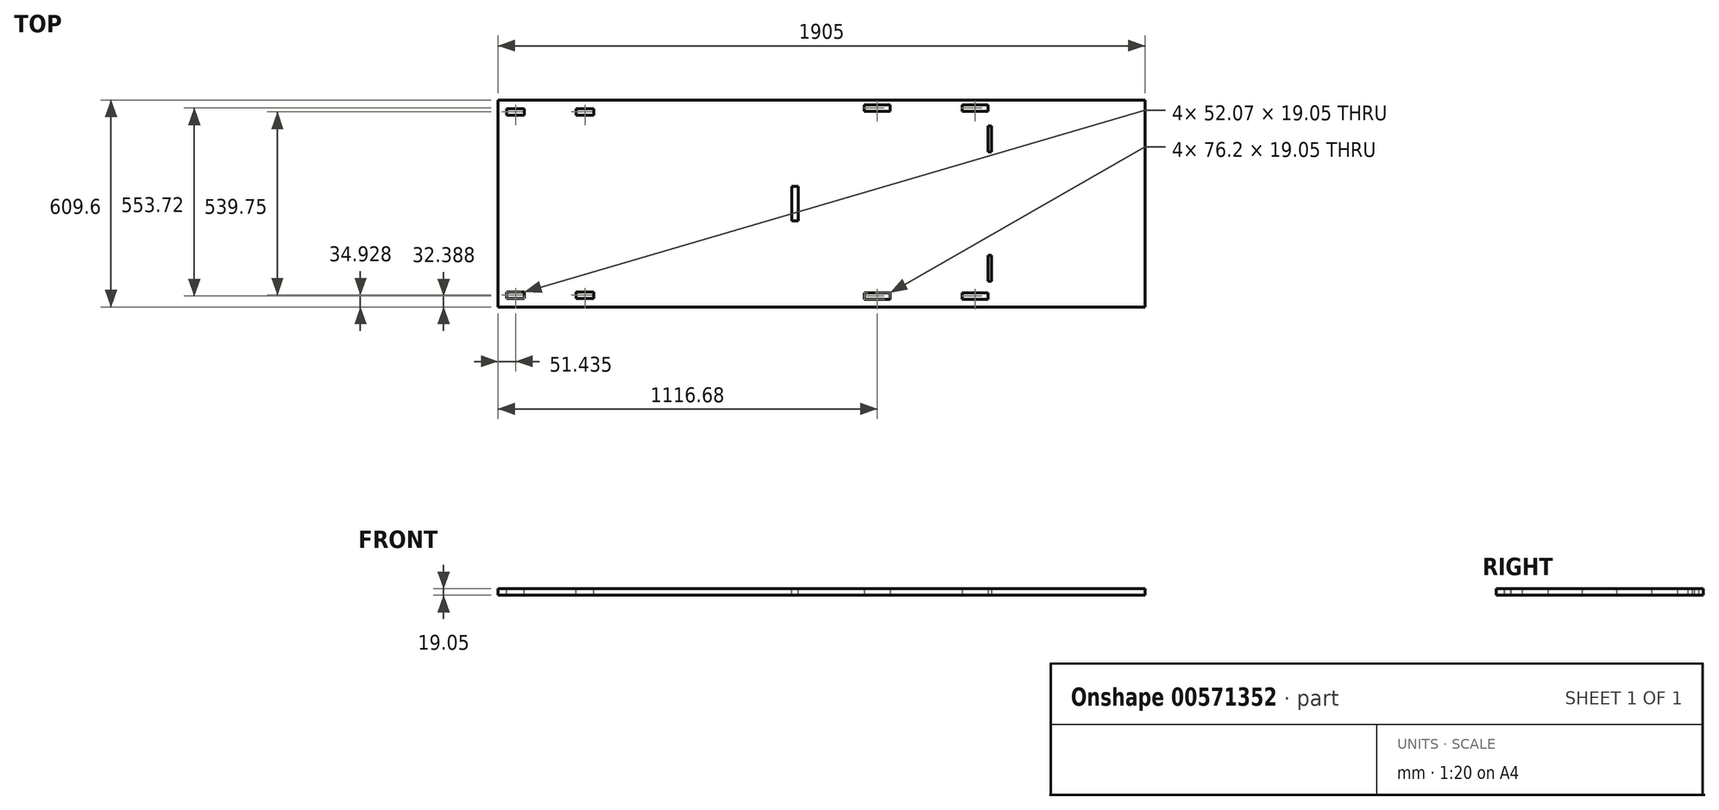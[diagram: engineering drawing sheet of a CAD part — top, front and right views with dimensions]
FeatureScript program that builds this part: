
annotation { "Feature Type Name" : "Feature", "Feature Type Description" : "" }
export const myFeature = defineFeature(function(context is Context, id is Id, definition is map)
    precondition{}
    {
        {
            var Q0;
            Q0=qCreatedBy(makeId("Top.planeOp"),FACE);
            var sketch = newSketch(context, id + "F0", { "sketchPlane" : qUnion([Q0])});
            skLineSegment(sketch, "E0.bottom", {"start": v(-750.92, 356.97) * mm, "end": v(1154.08, 356.97) * mm});
            skLineSegment(sketch, "E0.top", {"start": v(-750.92, -252.63) * mm, "end": v(1154.08, -252.63) * mm});
            skLineSegment(sketch, "E0.left", {"start": v(-750.92, 356.97) * mm, "end": v(-750.92, -252.63) * mm});
            skLineSegment(sketch, "E0.right", {"start": v(1154.08, 356.97) * mm, "end": v(1154.08, -252.63) * mm});
            skLineSegment(sketch, "E1", {"start": v(1154.08, 356.97) * mm, "end": v(696.88, 356.97) * mm});
            skLineSegment(sketch, "E2", {"start": v(691.34, 280.77) * mm, "end": v(691.34, 204.57) * mm});
            skLineSegment(sketch, "E3", {"start": v(701.5, 280.77) * mm, "end": v(701.5, 204.57) * mm});
            skLineSegment(sketch, "E4", {"start": v(691.34, 280.77) * mm, "end": v(701.5, 280.77) * mm});
            skLineSegment(sketch, "E5", {"start": v(691.34, 204.57) * mm, "end": v(701.5, 204.57) * mm});
            skLineSegment(sketch, "E6", {"start": v(701.5, -100.23) * mm, "end": v(701.5, -176.43) * mm});
            skLineSegment(sketch, "E7", {"start": v(691.34, -100.23) * mm, "end": v(691.34, -176.43) * mm});
            skLineSegment(sketch, "E8", {"start": v(691.34, -176.43) * mm, "end": v(701.5, -176.43) * mm});
            skLineSegment(sketch, "E9", {"start": v(691.34, -100.23) * mm, "end": v(701.5, -100.23) * mm});
            skLineSegment(sketch, "E10", {"start": v(696.88, 356.97) * mm, "end": v(239.68, 356.97) * mm});
            skLineSegment(sketch, "E11", {"start": v(696.88, -252.63) * mm, "end": v(239.68, -252.63) * mm});
            skLineSegment(sketch, "E12", {"start": v(-446.12, -252.63) * mm, "end": v(-446.12, 356.97) * mm});
            skLineSegment(sketch, "E13", {"start": v(615, 323.95) * mm, "end": v(615, 343) * mm});
            skLineSegment(sketch, "E14", {"start": v(615.6, -210.72) * mm, "end": v(691.8, -210.72) * mm});
            skLineSegment(sketch, "E15", {"start": v(615.6, -229.77) * mm, "end": v(691.8, -229.77) * mm});
            skLineSegment(sketch, "E16", {"start": v(615.6, -210.72) * mm, "end": v(615.6, -229.77) * mm});
            skLineSegment(sketch, "E17", {"start": v(691.8, -210.72) * mm, "end": v(691.8, -229.77) * mm});
            skLineSegment(sketch, "E18", {"start": v(615, 323.95) * mm, "end": v(691.2, 323.95) * mm});
            skLineSegment(sketch, "E19", {"start": v(615, 343) * mm, "end": v(691.2, 343) * mm});
            skLineSegment(sketch, "E20", {"start": v(691.2, 343) * mm, "end": v(691.2, 323.95) * mm});
            skLineSegment(sketch, "E21", {"start": v(403.86, 343) * mm, "end": v(327.66, 343) * mm});
            skLineSegment(sketch, "E22", {"start": v(327.66, 343) * mm, "end": v(327.66, 323.95) * mm});
            skLineSegment(sketch, "E23", {"start": v(327.66, 323.95) * mm, "end": v(403.86, 323.95) * mm});
            skLineSegment(sketch, "E24", {"start": v(403.86, 343) * mm, "end": v(403.86, 323.95) * mm});
            skLineSegment(sketch, "E25", {"start": v(403.86, -210.72) * mm, "end": v(327.66, -210.72) * mm});
            skLineSegment(sketch, "E26", {"start": v(327.66, -210.72) * mm, "end": v(327.66, -229.77) * mm});
            skLineSegment(sketch, "E27", {"start": v(403.86, -229.77) * mm, "end": v(327.66, -229.77) * mm});
            skLineSegment(sketch, "E28", {"start": v(403.86, -210.72) * mm, "end": v(403.86, -229.77) * mm});
            skSolve(sketch);
        }
        {
            var Q0;
            {var subQ0=sQuery(id+"F0.wireOp",EDGE,"E0.left");Q0=makeQuery(id+"F0.imprint","IMPRINT",FACE,{"disambiguationData":[TD([[makeQuery(id+"F0.imprint","IMPRINT",EDGE,{"derivedFrom":subQ0}),1.0]])]});}
            var Q1;
            {var subQ10=sQuery(id+"F0.wireOp",EDGE,"E2");Q1=makeQuery(id+"F0.imprint","IMPRINT",FACE,{"disambiguationData":[TD([[makeQuery(id+"F0.imprint","IMPRINT",EDGE,{"derivedFrom":subQ10}),-1.0]])]});}
            var Q2;
            {var subQ9=sQuery(id+"F0.wireOp",EDGE,"E0.right");Q2=makeQuery(id+"F0.imprint","IMPRINT",FACE,{"disambiguationData":[TD([[makeQuery(id+"F0.imprint","IMPRINT",EDGE,{"derivedFrom":subQ9}),-1.0]])]});}
            extrude(context, id + "F1", {"entities" : qUnion([Q0, Q1, Q2]), "depth" : 19.05 * mm, "offsetDistance" : 25.4 * mm});
        }
        {
            var Q0;
            Q0=makeQuery(id+"F1.opExtrude","CAP_FACE",FACE,{"disambiguationData":[OSD([sQuery(id+"F0.wireOp",EDGE,"E0.bottom"),sQuery(id+"F0.wireOp",EDGE,"E0.top"),sQuery(id+"F0.wireOp",EDGE,"E0.left"),sQuery(id+"F0.wireOp",EDGE,"E0.right"),sQuery(id+"F0.wireOp",EDGE,"E1"),sQuery(id+"F0.wireOp",EDGE,"E2"),sQuery(id+"F0.wireOp",EDGE,"E3"),sQuery(id+"F0.wireOp",EDGE,"E4"),sQuery(id+"F0.wireOp",EDGE,"E5"),sQuery(id+"F0.wireOp",EDGE,"E6"),sQuery(id+"F0.wireOp",EDGE,"E7"),sQuery(id+"F0.wireOp",EDGE,"E8"),sQuery(id+"F0.wireOp",EDGE,"E9"),sQuery(id+"F0.wireOp",EDGE,"E10"),sQuery(id+"F0.wireOp",EDGE,"E11"),sQuery(id+"F0.wireOp",EDGE,"QmkHj5L8-oyL5-zW05-RR0E-9zUQOD6hAJXw"),sQuery(id+"F0.wireOp",EDGE,"NXhRgJ8f-ZWsl-M3OL-PJf4-LyT9sPGGzkt8"),sQuery(id+"F0.wireOp",EDGE,"4B3FTJqG-diJZ-d2lG-Ft6A-RkHdd8seerWl"),sQuery(id+"F0.wireOp",EDGE,"R15m65rJ-UCmI-JcNw-TZQQ-C82T2MT2TRl5"),sQuery(id+"F0.wireOp",EDGE,"1eo9sw2a-eWhT-DOlG-EcZh-JO0kkJcUlVhu"),sQuery(id+"F0.wireOp",EDGE,"FfFJbHnD-gJYV-zVM3-fTFe-NOGbbAry73vU"),sQuery(id+"F0.wireOp",EDGE,"sL2tPH2F-Vb65-m7KG-u09N-uDdJG5wWwWGU"),sQuery(id+"F0.wireOp",EDGE,"YkzlyzqE-c5ER-Dy2x-MixH-OIeI8uiPQkjd"),sQuery(id+"F0.wireOp",EDGE,"NdCptRCe-83J5-WAEe-JwYB-HmezPEcczWWe"),sQuery(id+"F0.wireOp",EDGE,"bfdubq4F-wSr1-oBtw-IC4M-5gowiXU6hM2a"),sQuery(id+"F0.wireOp",EDGE,"JjW2KraA-f2yu-AIPd-Dusz-uy1x1c4ILi4Y"),sQuery(id+"F0.wireOp",EDGE,"OJAaXgpW-QYTT-vXd3-VglA-44XrmJkZB6MP"),sQuery(id+"F0.wireOp",EDGE,"3na8NIE6-NewC-HiAf-SF1q-UdVkwp7VlJ5b"),sQuery(id+"F0.wireOp",EDGE,"herUa8Bz-D43l-K3Ny-pNnq-0sttjwhlNGAH"),sQuery(id+"F0.wireOp",EDGE,"gqBFXKxU-2hC8-Fx8m-nDDS-Oiex3NbXzXUW"),sQuery(id+"F0.wireOp",EDGE,"a2ZStkuI-dOKN-J62b-Z5Fz-Vwy9hGdcItpk")])],"isStart":false});
            var sketch = newSketch(context, id + "F2", { "sketchPlane" : qUnion([Q0])});
            skLineSegment(sketch, "E29.0", {"start": v(691.34, 204.57) * mm, "end": v(701.5, 204.57) * mm});
            skLineSegment(sketch, "E30.0", {"start": v(691.34, -100.23) * mm, "end": v(701.5, -100.23) * mm});
            skLineSegment(sketch, "E31", {"start": v(691.34, -100.23) * mm, "end": v(691.34, 204.57) * mm});
            skLineSegment(sketch, "E32", {"start": v(691.34, 52.17) * mm, "end": v(132.54, 52.17) * mm});
            skLineSegment(sketch, "E33", {"start": v(132.54, 52.17) * mm, "end": v(132.54, 1.37) * mm});
            skLineSegment(sketch, "E34", {"start": v(132.54, 52.17) * mm, "end": v(132.54, 102.97) * mm});
            skLineSegment(sketch, "E35", {"start": v(132.54, 1.37) * mm, "end": v(113.49, 1.37) * mm});
            skLineSegment(sketch, "E36", {"start": v(132.54, 102.97) * mm, "end": v(113.49, 102.97) * mm});
            skLineSegment(sketch, "E37", {"start": v(113.49, 1.37) * mm, "end": v(113.49, 102.97) * mm});
            skSolve(sketch);
        }
        {
            var Q0;
            Q0=makeQuery(id+"F2.imprint","IMPRINT",FACE,{"disambiguationData":[TD([[makeQuery(id+"F2.imprint","IMPRINT",EDGE,{"derivedFrom":sQuery(id+"F2.wireOp",EDGE,"E33")}),-1.0]])]});
            extrude(context, id + "F3", {"entities" : qUnion([Q0]), "operationType" : NewBodyOperationType.REMOVE, "oppositeDirection" : true, "depth" : 19.05 * mm, "offsetDistance" : 25.4 * mm});
        }
        {
            var Q0;
            Q0=makeQuery(id+"F1.opExtrude","CAP_FACE",FACE,{"disambiguationData":[OSD([sQuery(id+"F0.wireOp",EDGE,"E0.bottom"),sQuery(id+"F0.wireOp",EDGE,"E0.top"),sQuery(id+"F0.wireOp",EDGE,"E0.left"),sQuery(id+"F0.wireOp",EDGE,"E0.right"),sQuery(id+"F0.wireOp",EDGE,"E1"),sQuery(id+"F0.wireOp",EDGE,"E2"),sQuery(id+"F0.wireOp",EDGE,"E3"),sQuery(id+"F0.wireOp",EDGE,"E4"),sQuery(id+"F0.wireOp",EDGE,"E5"),sQuery(id+"F0.wireOp",EDGE,"E6"),sQuery(id+"F0.wireOp",EDGE,"E7"),sQuery(id+"F0.wireOp",EDGE,"E8"),sQuery(id+"F0.wireOp",EDGE,"E9"),sQuery(id+"F0.wireOp",EDGE,"E10"),sQuery(id+"F0.wireOp",EDGE,"E11"),sQuery(id+"F0.wireOp",EDGE,"WTkWyY37-3lff-6tlJ-L3M8-YpPjWCgPXm64"),sQuery(id+"F0.wireOp",EDGE,"9uBbLRJS-CgFI-kPLr-TAIs-x9QxfTlsCxWZ"),sQuery(id+"F0.wireOp",EDGE,"p2a6MOfC-DApS-13w2-d2JD-gSqiaJMkhiBx"),sQuery(id+"F0.wireOp",EDGE,"IbED1Guz-II6V-0NPe-i4dc-zlwxUVHyGAy4"),sQuery(id+"F0.wireOp",EDGE,"Ath4HGWD-x2Cc-wjl7-hzrD-u5rLAHeANJgQ"),sQuery(id+"F0.wireOp",EDGE,"d7XaOh94-VqNg-hxHF-QjiW-E4eiPWdUFhtF"),sQuery(id+"F0.wireOp",EDGE,"f9zO5AK0-2Ykp-6dF4-tqWa-GQDSEDee3v7o"),sQuery(id+"F0.wireOp",EDGE,"UJLcTvZY-6Qv7-3I0p-XAdm-9oufj5vObeAg"),sQuery(id+"F0.wireOp",EDGE,"4nHZ0VxG-wd32-KUmD-eGWB-vXJI5H6IS5VK"),sQuery(id+"F0.wireOp",EDGE,"OGMhqHrC-eZiI-L9xN-popL-Ws3W6t9iTgra"),sQuery(id+"F0.wireOp",EDGE,"iE1YtSn0-DXz8-NUad-FM2E-uWIwMvyQOniF"),sQuery(id+"F0.wireOp",EDGE,"yRuZRdcb-78Xx-qdq1-8oNC-wYOMU3YOf1uJ"),sQuery(id+"F0.wireOp",EDGE,"0NzoH90u-ptvj-eGZD-e4ys-8rDY4hP88DKq"),sQuery(id+"F0.wireOp",EDGE,"lcbY2oca-XLyp-ZhzI-ta4P-xpIdYrPwBrTZ"),sQuery(id+"F0.wireOp",EDGE,"KJbxbycU-EoSs-WrZE-CX54-UYXhoAX5JvG9"),sQuery(id+"F0.wireOp",EDGE,"jgAFOijl-qdBJ-FO1S-SAlM-pBYE1SinQyUh")])],"isStart":false});
            var sketch = newSketch(context, id + "F4", { "sketchPlane" : qUnion([Q0])});
            skSolve(sketch);
        }
        {
            var Q0;
            Q0=makeQuery(id+"F1.opExtrude","CAP_FACE",FACE,{"disambiguationData":[OSD([sQuery(id+"F0.wireOp",EDGE,"E0.bottom"),sQuery(id+"F0.wireOp",EDGE,"E0.top"),sQuery(id+"F0.wireOp",EDGE,"E0.left"),sQuery(id+"F0.wireOp",EDGE,"E0.right"),sQuery(id+"F0.wireOp",EDGE,"E1"),sQuery(id+"F0.wireOp",EDGE,"E2"),sQuery(id+"F0.wireOp",EDGE,"E3"),sQuery(id+"F0.wireOp",EDGE,"E4"),sQuery(id+"F0.wireOp",EDGE,"E5"),sQuery(id+"F0.wireOp",EDGE,"E6"),sQuery(id+"F0.wireOp",EDGE,"E7"),sQuery(id+"F0.wireOp",EDGE,"E8"),sQuery(id+"F0.wireOp",EDGE,"E9"),sQuery(id+"F0.wireOp",EDGE,"E10"),sQuery(id+"F0.wireOp",EDGE,"E11"),sQuery(id+"F0.wireOp",EDGE,"WTkWyY37-3lff-6tlJ-L3M8-YpPjWCgPXm64"),sQuery(id+"F0.wireOp",EDGE,"9uBbLRJS-CgFI-kPLr-TAIs-x9QxfTlsCxWZ"),sQuery(id+"F0.wireOp",EDGE,"p2a6MOfC-DApS-13w2-d2JD-gSqiaJMkhiBx"),sQuery(id+"F0.wireOp",EDGE,"IbED1Guz-II6V-0NPe-i4dc-zlwxUVHyGAy4"),sQuery(id+"F0.wireOp",EDGE,"Ath4HGWD-x2Cc-wjl7-hzrD-u5rLAHeANJgQ"),sQuery(id+"F0.wireOp",EDGE,"d7XaOh94-VqNg-hxHF-QjiW-E4eiPWdUFhtF"),sQuery(id+"F0.wireOp",EDGE,"f9zO5AK0-2Ykp-6dF4-tqWa-GQDSEDee3v7o"),sQuery(id+"F0.wireOp",EDGE,"UJLcTvZY-6Qv7-3I0p-XAdm-9oufj5vObeAg"),sQuery(id+"F0.wireOp",EDGE,"4nHZ0VxG-wd32-KUmD-eGWB-vXJI5H6IS5VK"),sQuery(id+"F0.wireOp",EDGE,"OGMhqHrC-eZiI-L9xN-popL-Ws3W6t9iTgra"),sQuery(id+"F0.wireOp",EDGE,"iE1YtSn0-DXz8-NUad-FM2E-uWIwMvyQOniF"),sQuery(id+"F0.wireOp",EDGE,"yRuZRdcb-78Xx-qdq1-8oNC-wYOMU3YOf1uJ"),sQuery(id+"F0.wireOp",EDGE,"0NzoH90u-ptvj-eGZD-e4ys-8rDY4hP88DKq"),sQuery(id+"F0.wireOp",EDGE,"lcbY2oca-XLyp-ZhzI-ta4P-xpIdYrPwBrTZ"),sQuery(id+"F0.wireOp",EDGE,"KJbxbycU-EoSs-WrZE-CX54-UYXhoAX5JvG9"),sQuery(id+"F0.wireOp",EDGE,"jgAFOijl-qdBJ-FO1S-SAlM-pBYE1SinQyUh")])],"isStart":false});
            var sketch = newSketch(context, id + "F5", { "sketchPlane" : qUnion([Q0])});
            skLineSegment(sketch, "E38.0", {"start": v(-750.92, -252.63) * mm, "end": v(1055.91, -252.63) * mm});
            skLineSegment(sketch, "E39.0", {"start": v(-750.92, 356.97) * mm, "end": v(-750.92, -252.63) * mm});
            skSolve(sketch);
        }
        {
            var Q0;
            Q0=makeQuery(id+"F5.imprint","IMPRINT",FACE,{"disambiguationData":[TD([[makeQuery(id+"F5.imprint","IMPRINT",EDGE,{"derivedFrom":sQuery(id+"F5.wireOp",EDGE,"E38.0")}),1.0]])]});
            var sketch = newSketch(context, id + "F6", { "sketchPlane" : qUnion([Q0])});
            skLineSegment(sketch, "E40.0", {"start": v(-750.92, -252.63) * mm, "end": v(1055.91, -252.63) * mm});
            skLineSegment(sketch, "E41.0", {"start": v(-750.92, 356.97) * mm, "end": v(1055.91, 356.97) * mm});
            skLineSegment(sketch, "E42.0", {"start": v(-750.92, 356.97) * mm, "end": v(-750.92, -252.63) * mm});
            skLineSegment(sketch, "E43", {"start": v(-725.52, -252.63) * mm, "end": v(-725.52, -227.23) * mm});
            skLineSegment(sketch, "E44", {"start": v(-725.52, -227.23) * mm, "end": v(-673.45, -227.23) * mm});
            skLineSegment(sketch, "E45", {"start": v(-673.45, -227.23) * mm, "end": v(-673.45, -208.18) * mm});
            skLineSegment(sketch, "E46", {"start": v(-725.52, -227.23) * mm, "end": v(-725.52, -208.18) * mm});
            skLineSegment(sketch, "E47", {"start": v(-725.52, -208.18) * mm, "end": v(-673.45, -208.18) * mm});
            skLineSegment(sketch, "E48", {"start": v(-673.45, -227.23) * mm, "end": v(-521.05, -227.23) * mm});
            skLineSegment(sketch, "E49", {"start": v(-521.05, -227.23) * mm, "end": v(-521.05, -208.18) * mm});
            skLineSegment(sketch, "E50", {"start": v(-521.05, -227.23) * mm, "end": v(-468.98, -227.23) * mm});
            skLineSegment(sketch, "E51", {"start": v(-468.98, -227.23) * mm, "end": v(-468.98, -208.18) * mm});
            skLineSegment(sketch, "E52", {"start": v(-468.98, -208.18) * mm, "end": v(-521.05, -208.18) * mm});
            skLineSegment(sketch, "E53", {"start": v(-725.52, 356.97) * mm, "end": v(-725.52, 331.57) * mm});
            skLineSegment(sketch, "E54", {"start": v(-725.52, 331.57) * mm, "end": v(-673.45, 331.57) * mm});
            skLineSegment(sketch, "E55", {"start": v(-673.45, 331.57) * mm, "end": v(-673.45, 312.52) * mm});
            skLineSegment(sketch, "E56", {"start": v(-673.45, 312.52) * mm, "end": v(-725.52, 312.52) * mm});
            skLineSegment(sketch, "E57", {"start": v(-725.52, 312.52) * mm, "end": v(-725.52, 331.57) * mm});
            skLineSegment(sketch, "E58", {"start": v(-673.45, 331.57) * mm, "end": v(-521.05, 331.57) * mm});
            skLineSegment(sketch, "E59", {"start": v(-521.05, 331.57) * mm, "end": v(-521.05, 312.52) * mm});
            skLineSegment(sketch, "E60", {"start": v(-521.05, 312.52) * mm, "end": v(-468.98, 312.52) * mm});
            skLineSegment(sketch, "E61", {"start": v(-468.98, 312.52) * mm, "end": v(-468.98, 331.57) * mm});
            skLineSegment(sketch, "E62", {"start": v(-468.98, 331.57) * mm, "end": v(-521.05, 331.57) * mm});
            skSolve(sketch);
        }
        {
            var Q0;
            Q0=makeQuery(id+"F6.imprint","IMPRINT",FACE,{"disambiguationData":[TD([[makeQuery(id+"F6.imprint","IMPRINT",EDGE,{"derivedFrom":sQuery(id+"F6.wireOp",EDGE,"E44")}),1.0]])]});
            var Q1;
            Q1=makeQuery(id+"F6.imprint","IMPRINT",FACE,{"disambiguationData":[TD([[makeQuery(id+"F6.imprint","IMPRINT",EDGE,{"derivedFrom":sQuery(id+"F6.wireOp",EDGE,"E49")}),-1.0]])]});
            var Q2;
            Q2=makeQuery(id+"F6.imprint","IMPRINT",FACE,{"disambiguationData":[TD([[makeQuery(id+"F6.imprint","IMPRINT",EDGE,{"derivedFrom":sQuery(id+"F6.wireOp",EDGE,"E59")}),1.0]])]});
            var Q3;
            Q3=makeQuery(id+"F6.imprint","IMPRINT",FACE,{"disambiguationData":[TD([[makeQuery(id+"F6.imprint","IMPRINT",EDGE,{"derivedFrom":sQuery(id+"F6.wireOp",EDGE,"E54")}),-1.0]])]});
            extrude(context, id + "F7", {"entities" : qUnion([Q0, Q1, Q2, Q3]), "operationType" : NewBodyOperationType.REMOVE, "oppositeDirection" : true, "depth" : 19.05 * mm, "offsetDistance" : 25.4 * mm});
        }
    });
